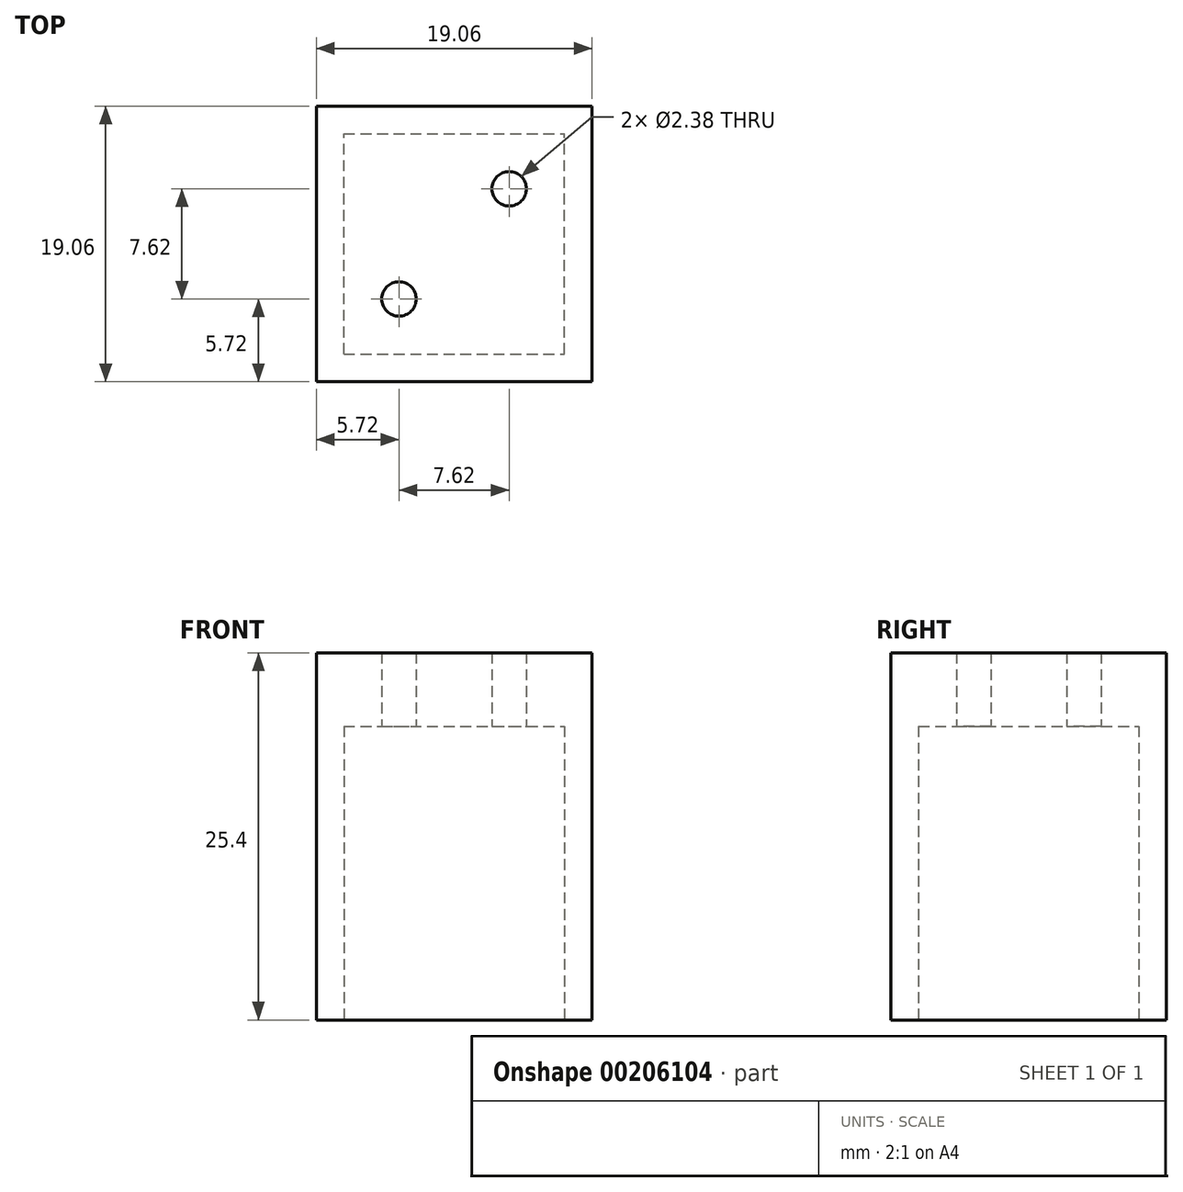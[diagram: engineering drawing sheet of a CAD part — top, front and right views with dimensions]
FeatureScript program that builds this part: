
annotation { "Feature Type Name" : "Feature", "Feature Type Description" : "" }
export const myFeature = defineFeature(function(context is Context, id is Id, definition is map)
    precondition{}
    {
        {
            var Q0;
            Q0=qCreatedBy(makeId("Front.planeOp"),FACE);
            var sketch = newSketch(context, id + "F0", { "sketchPlane" : qUnion([Q0])});
            skLineSegment(sketch, "E0.bottom", {"start": v(-9.52, 12.7) * mm, "end": v(9.53, 12.7) * mm});
            skLineSegment(sketch, "E0.top", {"start": v(-9.53, -12.7) * mm, "end": v(9.52, -12.7) * mm});
            skLineSegment(sketch, "E0.left", {"start": v(-9.52, 12.7) * mm, "end": v(-9.53, -12.7) * mm});
            skLineSegment(sketch, "E0.right", {"start": v(9.53, 12.7) * mm, "end": v(9.52, -12.7) * mm});
            skPoint(sketch, "E0.middle", {"position": v(0, 0) * mm});
            skLineSegment(sketch, "E1", {"start": v(9.53, 7.62) * mm, "end": v(9.53, 12.7) * mm});
            skSolve(sketch);
        }
        {
            var Q0;
            Q0 = qSketchRegion(id + "F0", true);
            extrude(context, id + "F1", {"entities" : qUnion([Q0]), "endBound" : BoundingType.SYMMETRIC, "depth" : 19.05 * mm});
        }
        {
            var Q0;
            Q0=makeQuery(id+"F1.opExtrude","SWEPT_FACE",FACE,{"disambiguationData":[OSD([sQuery(id+"F0.wireOp",EDGE,"E0.top")])]});
            var sketch = newSketch(context, id + "F2", { "sketchPlane" : qUnion([Q0])});
            skLineSegment(sketch, "E2.bottom", {"start": v(-7.62, 7.62) * mm, "end": v(7.62, 7.62) * mm});
            skLineSegment(sketch, "E2.top", {"start": v(-7.62, -7.62) * mm, "end": v(7.62, -7.62) * mm});
            skLineSegment(sketch, "E2.left", {"start": v(-7.62, 7.62) * mm, "end": v(-7.62, -7.62) * mm});
            skLineSegment(sketch, "E2.right", {"start": v(7.62, 7.62) * mm, "end": v(7.62, -7.62) * mm});
            skPoint(sketch, "E2.middle", {"position": v(0, 0) * mm});
            skSolve(sketch);
        }
        {
            var Q0;
            Q0 = qSketchRegion(id + "F2", true);
            extrude(context, id + "F3", {"entities" : qUnion([Q0]), "operationType" : NewBodyOperationType.REMOVE, "oppositeDirection" : true, "depth" : 20.32 * mm});
        }
        {
            var Q0;
            Q0=makeQuery(id+"F3.boolean.opBoolean","COPY",FACE,{"derivedFrom":makeQuery(id+"F3.opExtrude","CAP_FACE",FACE,{"disambiguationData":[OSD([sQuery(id+"F2.wireOp",EDGE,"E2.bottom"),sQuery(id+"F2.wireOp",EDGE,"E2.top"),sQuery(id+"F2.wireOp",EDGE,"E2.left"),sQuery(id+"F2.wireOp",EDGE,"E2.right")])],"isStart":false})});
            var sketch = newSketch(context, id + "F4", { "sketchPlane" : qUnion([Q0])});
            skLineSegment(sketch, "E3", {"start": v(-7.62, 7.62) * mm, "end": v(0, 0) * mm});
            skLineSegment(sketch, "E4", {"start": v(0, 0) * mm, "end": v(7.62, -7.62) * mm});
            skCircle(sketch, "E5", {"center": v(-3.81, 3.8) * mm, "radius": 1.79 * mm});
            skCircle(sketch, "E6", {"center": v(3.81, -3.8) * mm, "radius": 1.79 * mm});
            skCircle(sketch, "E7", {"center": v(-3.81, 3.8) * mm, "radius": 2.38 * mm});
            skCircle(sketch, "E8", {"center": v(3.81, -3.8) * mm, "radius": 2.51 * mm});
            skSolve(sketch);
        }
        {
            var Q0;
            Q0=sQuery(id+"F4.wireOp",VERTEX,"E5.center");
            var Q1;
            Q1=sQuery(id+"F4.wireOp",VERTEX,"E6.center");
            var Q2;
            Q2=makeQuery(id+"F1.opExtrude","SWEPT_BODY",BODY,{"disambiguationData":[OSD([sQuery(id+"F0.wireOp",EDGE,"E0.bottom"),sQuery(id+"F0.wireOp",EDGE,"E0.top"),sQuery(id+"F0.wireOp",EDGE,"E0.left"),sQuery(id+"F0.wireOp",EDGE,"E0.right"),sQuery(id+"F0.wireOp",EDGE,"E1")])]});
            hole(context, id + "F5", {"style" : HoleStyle.SIMPLE, "endStyle" : HoleEndStyle.THROUGH, "holeDiameter" : 2.38 * mm, "locations" : qUnion([Q0, Q1]), "scope" : qUnion([Q2]), "isTappedThrough" : true});
        }
    });
